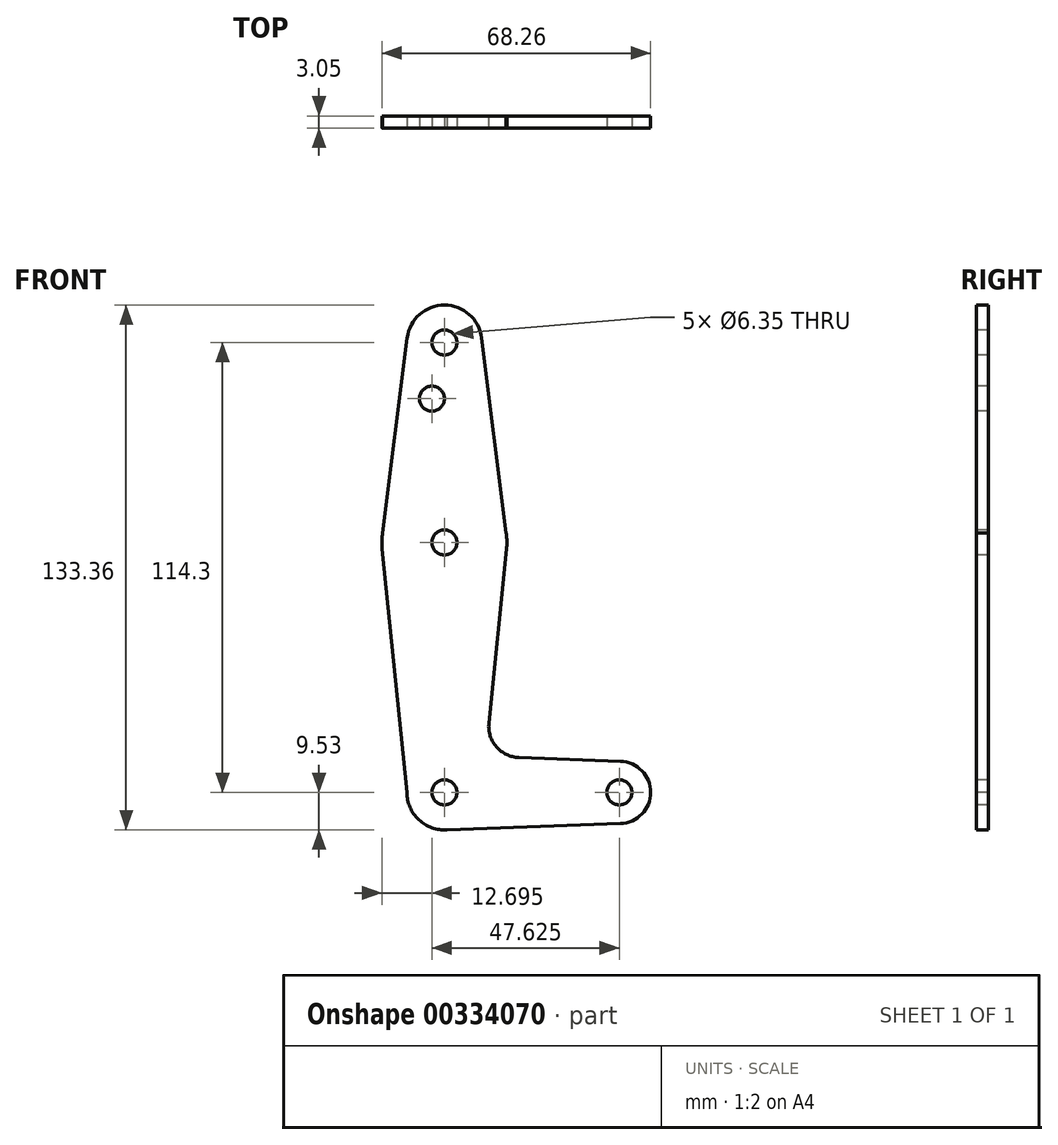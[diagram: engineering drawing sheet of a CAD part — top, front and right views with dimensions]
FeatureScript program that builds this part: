
annotation { "Feature Type Name" : "Feature", "Feature Type Description" : "" }
export const myFeature = defineFeature(function(context is Context, id is Id, definition is map)
    precondition{}
    {
        {
            var Q0;
            Q0=qCreatedBy(makeId("Front.planeOp"),FACE);
            var sketch = newSketch(context, id + "F0", { "sketchPlane" : qUnion([Q0])});
            skLineSegment(sketch, "E0", {"start": v(0, 0) * mm, "end": v(0, 114.3) * mm, "construction": true});
            skLineSegment(sketch, "E1", {"start": v(0, 0) * mm, "end": v(44.45, 0) * mm, "construction": true});
            skCircle(sketch, "E2", {"center": v(0, 114.3) * mm, "radius": 9.53 * mm});
            skCircle(sketch, "E3", {"center": v(0, 63.5) * mm, "radius": 15.88 * mm});
            skCircle(sketch, "E4", {"center": v(0, 0) * mm, "radius": 9.53 * mm});
            skCircle(sketch, "E5", {"center": v(44.45, 0) * mm, "radius": 7.94 * mm});
            skLineSegment(sketch, "E6", {"start": v(11.3, 17.6) * mm, "end": v(15.8, 61.9) * mm});
            skLineSegment(sketch, "E7", {"start": v(-9.52, 0) * mm, "end": v(-15.8, 61.9) * mm});
            skLineSegment(sketch, "E8", {"start": v(15.8, 65.1) * mm, "end": v(9.45, 115.49) * mm});
            skLineSegment(sketch, "E9", {"start": v(18.93, 8.85) * mm, "end": v(44.73, 7.93) * mm});
            skLineSegment(sketch, "E10", {"start": v(0, -9.53) * mm, "end": v(44.73, -7.93) * mm});
            skCircle(sketch, "E11", {"center": v(-3.18, 100.03) * mm, "radius": 3.18 * mm});
            skCircle(sketch, "E12", {"center": v(0, 63.5) * mm, "radius": 3.18 * mm});
            skCircle(sketch, "E13", {"center": v(0, 114.3) * mm, "radius": 3.18 * mm});
            skCircle(sketch, "E14", {"center": v(0, 0) * mm, "radius": 3.18 * mm});
            skCircle(sketch, "E15", {"center": v(44.45, 0) * mm, "radius": 3.18 * mm});
            skArc(sketch, "E16.filletArc", {"start": v(11.3, 17.6) * mm, "mid": v(13.22, 11.57) * mm, "end": v(18.93, 8.85) * mm});
            skLineSegment(sketch, "E17", {"start": v(-15.8, 65.1) * mm, "end": v(-9.45, 115.49) * mm});
            skSolve(sketch);
        }
        {
            var Q0;
            Q0 = qSketchRegion(id + "F0", true);
            extrude(context, id + "F1", {"entities" : qUnion([Q0]), "oppositeDirection" : true, "depth" : 3.05 * mm});
        }
    });
